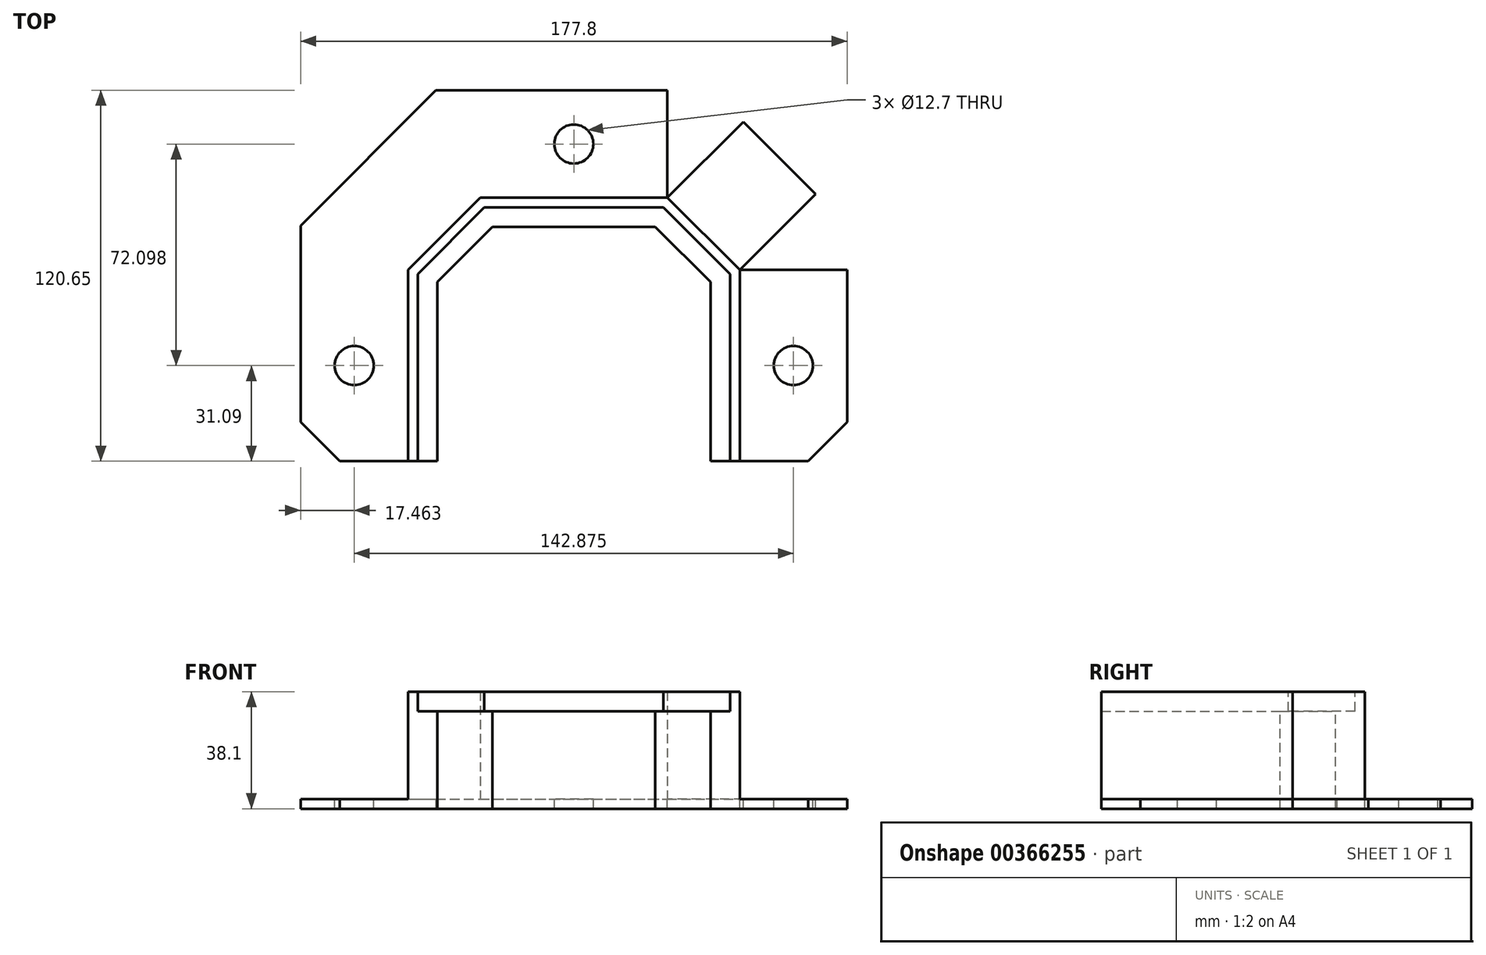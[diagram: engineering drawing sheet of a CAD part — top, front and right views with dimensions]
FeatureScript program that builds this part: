
annotation { "Feature Type Name" : "Feature", "Feature Type Description" : "" }
export const myFeature = defineFeature(function(context is Context, id is Id, definition is map)
    precondition{}
    {
        {
            var Q0;
            Q0=qCreatedBy(makeId("Front.planeOp"),FACE);
            var sketch = newSketch(context, id + "F0", { "sketchPlane" : qUnion([Q0])});
            skLineSegment(sketch, "E0.bottom", {"start": v(-53.98, 38.1) * mm, "end": v(-50.8, 38.1) * mm});
            skLineSegment(sketch, "E0.top", {"start": v(-53.98, 0) * mm, "end": v(-50.8, 0) * mm});
            skLineSegment(sketch, "E0.left", {"start": v(-53.98, 38.1) * mm, "end": v(-53.98, 3.18) * mm});
            skLineSegment(sketch, "E0.right", {"start": v(-50.8, 38.1) * mm, "end": v(-50.8, 0) * mm});
            skLineSegment(sketch, "E1.bottom", {"start": v(-50.8, 0) * mm, "end": v(-88.9, 0) * mm});
            skLineSegment(sketch, "E1.top", {"start": v(-53.98, 3.18) * mm, "end": v(-88.9, 3.17) * mm});
            skLineSegment(sketch, "E1.left", {"start": v(-50.8, 0) * mm, "end": v(-50.8, 3.18) * mm});
            skLineSegment(sketch, "E1.right", {"start": v(-88.9, 0) * mm, "end": v(-88.9, 3.17) * mm});
            skLineSegment(sketch, "E2.bottom", {"start": v(-50.8, 31.75) * mm, "end": v(-44.45, 31.75) * mm});
            skLineSegment(sketch, "E2.top", {"start": v(-50.8, 0) * mm, "end": v(-44.45, 0) * mm});
            skLineSegment(sketch, "E2.left", {"start": v(-50.8, 31.75) * mm, "end": v(-50.8, 0) * mm});
            skLineSegment(sketch, "E2.right", {"start": v(-44.45, 31.75) * mm, "end": v(-44.45, 0) * mm});
            skSolve(sketch);
        }
        {
            var Q0;
            Q0=qCreatedBy(makeId("Top.planeOp"),FACE);
            var sketch = newSketch(context, id + "F1", { "sketchPlane" : qUnion([Q0])});
            skLineSegment(sketch, "E3.top", {"start": v(-26.49, 76.2) * mm, "end": v(26.49, 76.2) * mm});
            skLineSegment(sketch, "E3.left", {"start": v(-44.45, 0) * mm, "end": v(-44.45, 58.24) * mm});
            skLineSegment(sketch, "E3.right", {"start": v(44.45, 0) * mm, "end": v(44.45, 58.24) * mm});
            skPoint(sketch, "E4.visualSharp", {"position": v(-44.45, 76.2) * mm});
            skPoint(sketch, "E5.visualSharp", {"position": v(44.45, 76.2) * mm});
            skLineSegment(sketch, "E6", {"start": v(-44.45, 58.24) * mm, "end": v(-26.49, 76.2) * mm});
            skLineSegment(sketch, "E7.MirrorCS", {"start": v(44.45, 58.24) * mm, "end": v(26.49, 76.2) * mm});
            skSolve(sketch);
        }
        {
            var Q0;
            Q0 = qSketchRegion(id + "F0", true);
            var Q1;
            Q1=sQuery(id+"F1.wireOp",EDGE,"E3.left");
            var Q2;
            Q2=sQuery(id+"F1.wireOp",EDGE,"E3.top");
            var Q3;
            Q3=sQuery(id+"F1.wireOp",EDGE,"E3.right");
            var Q4;
            Q4 = qConstructionFilter(qBodyType(qCreatedBy(id + "F1" ,EDGE), BodyType.WIRE), ConstructionObject.NO);
            sweep(context, id + "F2", {"profiles" : qUnion([Q0]), "surfaceProfiles" : qUnion([Q1, Q2, Q3]), "path" : qUnion([Q4])});
        }
        {
            var Q0;
            {var subQ1=sQuery(id+"F1.wireOp",EDGE,"E3.left");var subQ2=sQuery(id+"F0.wireOp",EDGE,"E1.top");var subQ3=makeQuery(id+"F2.opSweep","SWEPT_FACE",FACE,{"disambiguationData":[OSD([subQ2,subQ1])]});Q0=makeQuery(id+"FsdeTfMGCdAQ68a_1.boolean.opBoolean","SPLIT",FACE,{"disambiguationData":[TD([makeQuery(id+"FsdeTfMGCdAQ68a_1.opExtrude","SWEPT_FACE",FACE,{"disambiguationData":[OSD([sQuery(id+"F1Kq2kBcWs1gT9r_1.wireOp",EDGE,"c8BC0J2p-vvEX-Ohvj-JZ7o-ac5Rmsad9Ox0")])]})])],"derivedFrom":subQ3});}
            var sketch = newSketch(context, id + "F3", { "sketchPlane" : qUnion([Q0])});
            skPoint(sketch, "E8", {"position": v(-71.44, 31.09) * mm});
            skPoint(sketch, "E9.MirrorP", {"position": v(71.44, 31.09) * mm});
            skPoint(sketch, "E10", {"position": v(0, 103.19) * mm});
            skSolve(sketch);
        }
        {
            var Q0;
            Q0=sQuery(id+"F3.wireOp",VERTEX,"E8");
            var Q1;
            Q1=sQuery(id+"F3.wireOp",VERTEX,"6810d8a6-d159-4a82-9c21-2299b162ad55");
            var Q2;
            Q2=sQuery(id+"F3.wireOp",VERTEX,"E9.MirrorP");
            var Q3;
            Q3=sQuery(id+"F3.wireOp",VERTEX,"0093c1d9-3cf5-479a-8fd4-5f16fcd31b0d");
            var Q4;
            Q4=sQuery(id+"F3.wireOp",VERTEX,"ce83e92b-f1ba-4415-89fd-56c535c607b50.MirrorP");
            var Q5;
            Q5=sQuery(id+"F3.wireOp",VERTEX,"E10");
            var Q6;
            Q6=makeQuery(id+"F2.opSweep","SWEPT_BODY",BODY,{"disambiguationData":[OSD([sQuery(id+"F0.wireOp",EDGE,"E0.bottom"),sQuery(id+"F0.wireOp",EDGE,"E0.left"),sQuery(id+"F0.wireOp",EDGE,"E0.right"),sQuery(id+"F0.wireOp",EDGE,"E1.bottom"),sQuery(id+"F0.wireOp",EDGE,"E1.top"),sQuery(id+"F0.wireOp",EDGE,"E1.right"),sQuery(id+"F0.wireOp",EDGE,"E2.bottom"),sQuery(id+"F0.wireOp",EDGE,"E2.top"),sQuery(id+"F0.wireOp",EDGE,"E2.right"),sQuery(id+"F1.wireOp",EDGE,"E3.left")])]});
            hole(context, id + "F4", {"style" : HoleStyle.SIMPLE, "endStyle" : HoleEndStyle.BLIND, "holeDiameter" : 12.7 * mm, "holeDepth" : 12.7 * mm, "isTappedThrough" : true, "tappedDepth" : 9.52 * mm, "tapClearance" : 3, "locations" : qUnion([Q0, Q1, Q2, Q3, Q4, Q5]), "scope" : qUnion([Q6])});
        }
        {
            var Q0;
            Q0=makeQuery(id+"F2.opSweep","SWEPT_FACE",FACE,{"disambiguationData":[OSD([sQuery(id+"F0.wireOp",EDGE,"E1.top"),sQuery(id+"F1.wireOp",EDGE,"E3.left")])]});
            var sketch = newSketch(context, id + "F5", { "sketchPlane" : qUnion([Q0])});
            skLineSegment(sketch, "E11", {"start": v(-53.98, 62.18) * mm, "end": v(-88.9, 62.18) * mm});
            skLineSegment(sketch, "E12", {"start": v(-88.9, 62.18) * mm, "end": v(-53.98, 62.18) * mm});
            skLineSegment(sketch, "E13", {"start": v(-53.98, 62.18) * mm, "end": v(-78.67, 86.88) * mm});
            skLineSegment(sketch, "E14", {"start": v(-78.67, 86.88) * mm, "end": v(-53.98, 62.18) * mm});
            skLineSegment(sketch, "E15", {"start": v(-30.43, 85.72) * mm, "end": v(-55.13, 110.42) * mm});
            skLineSegment(sketch, "E16", {"start": v(-55.13, 110.42) * mm, "end": v(-30.43, 85.72) * mm});
            skLineSegment(sketch, "E17", {"start": v(-30.43, 120.65) * mm, "end": v(-30.43, 85.72) * mm});
            skLineSegment(sketch, "E18.MirrorCS", {"start": v(30.43, 120.65) * mm, "end": v(30.43, 85.72) * mm});
            skLineSegment(sketch, "E19.MirrorCS", {"start": v(55.13, 110.42) * mm, "end": v(30.43, 85.72) * mm});
            skLineSegment(sketch, "E20.MirrorCS", {"start": v(78.67, 86.88) * mm, "end": v(53.98, 62.18) * mm});
            skLineSegment(sketch, "E21.MirrorCS", {"start": v(88.9, 62.18) * mm, "end": v(53.98, 62.18) * mm});
            skSolve(sketch);
        }
        {
            var Q0;
            {var subQ0=sQuery(id+"F5.wireOp",EDGE,"E12");Q0=makeQuery(id+"F5.imprint","IMPRINT",FACE,{"disambiguationData":[TD([[makeQuery(id+"F5.imprint","IMPRINT",EDGE,{"derivedFrom":subQ0}),1.0]])]});}
            var Q1;
            {var subQ0=sQuery(id+"F5.wireOp",EDGE,"E16");Q1=makeQuery(id+"F5.imprint","IMPRINT",FACE,{"disambiguationData":[TD([[makeQuery(id+"F5.imprint","IMPRINT",EDGE,{"derivedFrom":subQ0}),1.0]])]});}
            var Q2;
            {var subQ0=sQuery(id+"F5.wireOp",EDGE,"E18.MirrorCS");Q2=makeQuery(id+"F5.imprint","IMPRINT",FACE,{"disambiguationData":[TD([[makeQuery(id+"F5.imprint","IMPRINT",EDGE,{"derivedFrom":subQ0}),1.0]])]});}
            var Q3;
            {var subQ0=sQuery(id+"F5.wireOp",EDGE,"E20.MirrorCS");Q3=makeQuery(id+"F5.imprint","IMPRINT",FACE,{"disambiguationData":[TD([[makeQuery(id+"F5.imprint","IMPRINT",EDGE,{"derivedFrom":subQ0}),1.0]])]});}
            extrude(context, id + "F6", {"entities" : qUnion([Q0, Q1, Q2, Q3]), "operationType" : NewBodyOperationType.REMOVE, "endBound" : BoundingType.THROUGH_ALL, "oppositeDirection" : true, "depth" : 25.4 * mm});
        }
        {
            var Q0;
            Q0=makeQuery(id+"F2.opSweep","CAP_EDGE",EDGE,{"disambiguationData":[OSD([sQuery(id+"F0.wireOp",EDGE,"E1.right"),sQuery(id+"F1.wireOp",VERTEX,"E3.left.start")])],"isStart":true});
            var Q1;
            Q1=makeQuery(id+"F2.opSweep","CAP_EDGE",EDGE,{"disambiguationData":[OSD([sQuery(id+"F0.wireOp",EDGE,"E1.right"),sQuery(id+"F1.wireOp",VERTEX,"E3.right.start")])],"isStart":false});
            chamfer(context, id + "F7", {"entities" : qUnion([Q0, Q1]), "width" : 12.7 * mm, "tangentPropagation" : true});
        }
    });
